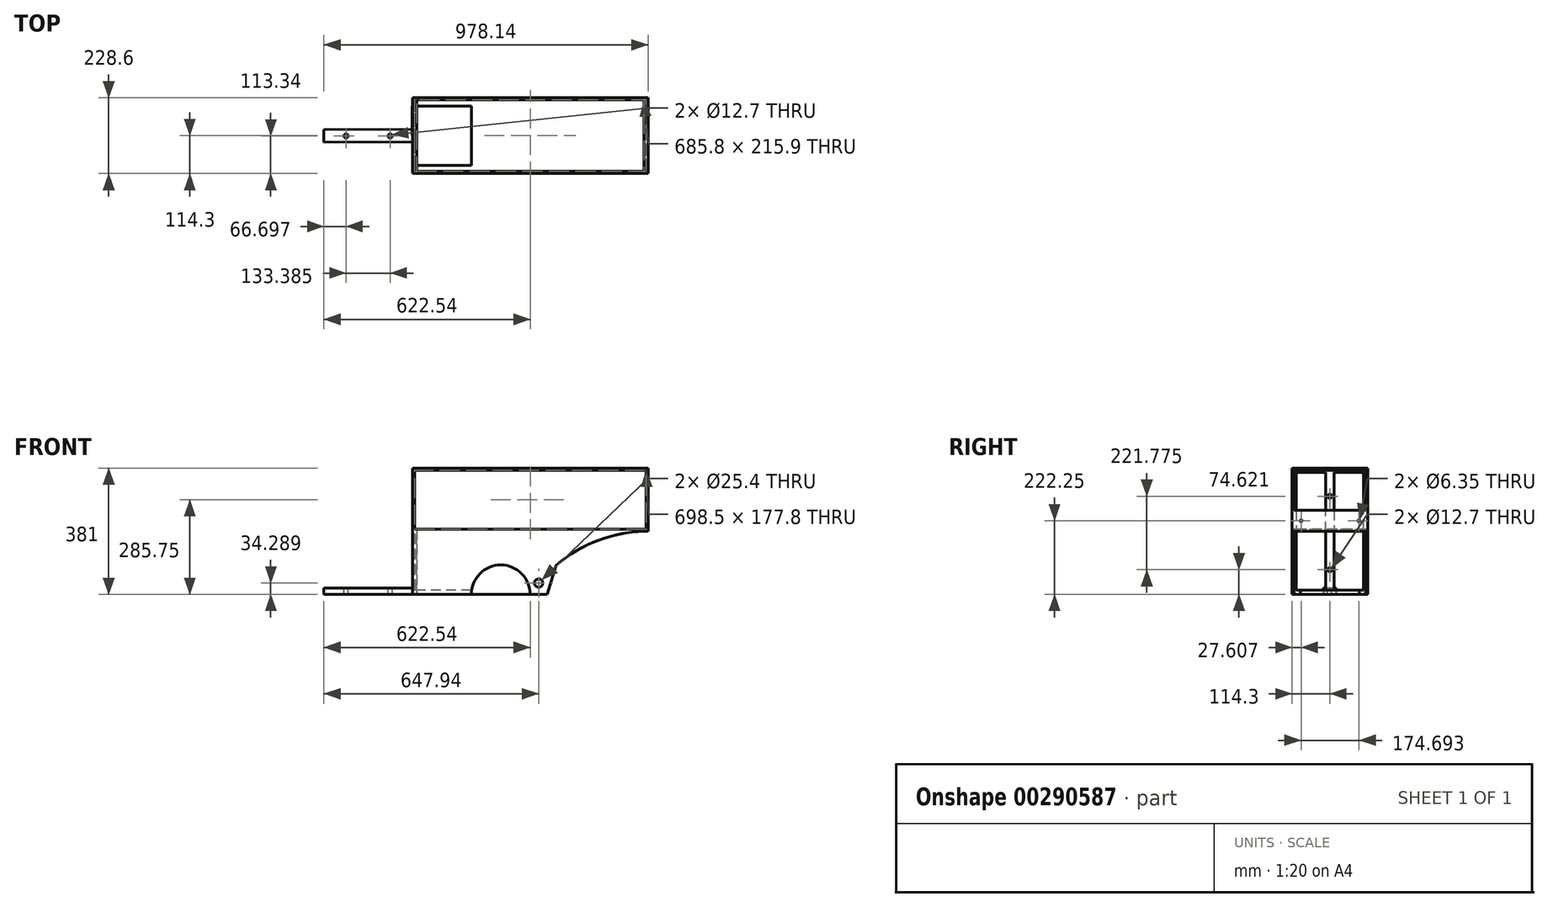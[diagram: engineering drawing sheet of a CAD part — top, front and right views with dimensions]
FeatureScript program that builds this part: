
annotation { "Feature Type Name" : "Feature", "Feature Type Description" : "" }
export const myFeature = defineFeature(function(context is Context, id is Id, definition is map)
    precondition{}
    {
        {
            var Q0;
            Q0=qCreatedBy(makeId("Top.planeOp"),FACE);
            var sketch = newSketch(context, id + "F0", { "sketchPlane" : qUnion([Q0])});
            skLineSegment(sketch, "E0.bottom", {"start": v(-355.6, 114.3) * mm, "end": v(355.6, 114.3) * mm});
            skLineSegment(sketch, "E0.top", {"start": v(-355.6, -114.3) * mm, "end": v(355.6, -114.3) * mm});
            skLineSegment(sketch, "E0.left", {"start": v(-355.6, 114.3) * mm, "end": v(-355.6, -114.3) * mm});
            skLineSegment(sketch, "E0.right", {"start": v(355.6, 114.3) * mm, "end": v(355.6, -114.3) * mm});
            skPoint(sketch, "E0.middle", {"position": v(0, 0) * mm});
            skLineSegment(sketch, "E1.bottom", {"start": v(-342.9, 107.95) * mm, "end": v(342.9, 107.95) * mm});
            skLineSegment(sketch, "E1.top", {"start": v(-342.9, -107.95) * mm, "end": v(342.9, -107.95) * mm});
            skLineSegment(sketch, "E1.left", {"start": v(-342.9, 107.95) * mm, "end": v(-342.9, -107.95) * mm});
            skLineSegment(sketch, "E1.right", {"start": v(342.9, 107.95) * mm, "end": v(342.9, -107.95) * mm});
            skSolve(sketch);
        }
        {
            var Q0;
            Q0=makeQuery(id+"F0.imprint","IMPRINT",FACE,{"disambiguationData":[TD([[makeQuery(id+"F0.imprint","IMPRINT",EDGE,{"derivedFrom":sQuery(id+"F0.wireOp",EDGE,"E0.bottom")}),-1.0]])]});
            extrude(context, id + "F1", {"entities" : qUnion([Q0]), "depth" : 381 * mm});
        }
        {
            var Q0;
            Q0=makeQuery(id+"F1.opExtrude","SWEPT_FACE",FACE,{"disambiguationData":[OSD([sQuery(id+"F0.wireOp",EDGE,"E0.top")])]});
            var sketch = newSketch(context, id + "F2", { "sketchPlane" : qUnion([Q0])});
            skLineSegment(sketch, "E2", {"start": v(-355.6, 381) * mm, "end": v(-355.6, 190.5) * mm, "construction": true});
            skLineSegment(sketch, "E3", {"start": v(-355.6, 190.5) * mm, "end": v(355.6, 190.5) * mm, "construction": true});
            skLineSegment(sketch, "E4", {"start": v(355.6, 190.5) * mm, "end": v(355.6, 381) * mm, "construction": true});
            skLineSegment(sketch, "E5", {"start": v(355.6, 381) * mm, "end": v(355.6, 0) * mm, "construction": true});
            skLineSegment(sketch, "E6", {"start": v(355.6, 0) * mm, "end": v(-355.6, 0) * mm, "construction": true});
            skLineSegment(sketch, "E7", {"start": v(-355.6, 0) * mm, "end": v(-355.6, 190.5) * mm, "construction": true});
            skLineSegment(sketch, "E8", {"start": v(-355.6, 381) * mm, "end": v(355.6, 381) * mm, "construction": true});
            skLineSegment(sketch, "E9", {"start": v(0, 190.5) * mm, "end": v(0, 381) * mm, "construction": true});
            skLineSegment(sketch, "E10", {"start": v(0, 381) * mm, "end": v(0, 0) * mm, "construction": true});
            skLineSegment(sketch, "E11", {"start": v(0, 0) * mm, "end": v(-355.6, 0) * mm, "construction": true});
            skLineSegment(sketch, "E12", {"start": v(-177.8, 0) * mm, "end": v(-177.8, 381) * mm, "construction": true});
            skLineSegment(sketch, "E13", {"start": v(-177.8, 381) * mm, "end": v(0, 381) * mm, "construction": true});
            skLineSegment(sketch, "E14", {"start": v(355.6, 381) * mm, "end": v(0, 381) * mm, "construction": true});
            skLineSegment(sketch, "E15", {"start": v(177.8, 381) * mm, "end": v(177.8, 0) * mm, "construction": true});
            skArc(sketch, "E16", {"start": v(355.6, 190.5) * mm, "mid": v(153.9, 139.87) * mm, "end": v(0, 0) * mm});
            skLineSegment(sketch, "E17.bottom", {"start": v(-349.25, 374.65) * mm, "end": v(349.25, 374.65) * mm});
            skLineSegment(sketch, "E17.top", {"start": v(-349.25, 238.03) * mm, "end": v(349.25, 238.03) * mm});
            skLineSegment(sketch, "E17.left", {"start": v(-349.25, 374.65) * mm, "end": v(-349.25, 238.03) * mm});
            skLineSegment(sketch, "E17.right", {"start": v(349.25, 374.65) * mm, "end": v(349.25, 238.03) * mm});
            skSolve(sketch);
        }
        {
            var Q0;
            Q0=makeQuery(id+"F2.imprint","IMPRINT",FACE,{"disambiguationData":[TD([[makeQuery(id+"F2.imprint","IMPRINT",EDGE,{"derivedFrom":sQuery(id+"F2.wireOp",EDGE,"E17.bottom")}),-1.0]])]});
            extrude(context, id + "F3", {"entities" : qUnion([Q0]), "operationType" : NewBodyOperationType.REMOVE, "endBound" : BoundingType.SYMMETRIC, "oppositeDirection" : true, "depth" : 381 * mm});
        }
        {
            var Q0;
            {var subQ0=sQuery(id+"F2.wireOp",EDGE,"E16");Q0=makeQuery(id+"F2.imprint","IMPRINT",FACE,{"disambiguationData":[TD([[makeQuery(id+"F2.imprint","IMPRINT",EDGE,{"derivedFrom":subQ0}),1.0]])]});}
            extrude(context, id + "F4", {"entities" : qUnion([Q0]), "operationType" : NewBodyOperationType.REMOVE, "endBound" : BoundingType.SYMMETRIC, "oppositeDirection" : true, "depth" : 508 * mm});
        }
        {
            var Q0;
            Q0=makeQuery(id+"F1.opExtrude","SWEPT_FACE",FACE,{"disambiguationData":[OSD([sQuery(id+"F0.wireOp",EDGE,"E0.left")])]});
            var sketch = newSketch(context, id + "F5", { "sketchPlane" : qUnion([Q0])});
            skLineSegment(sketch, "E18.bottom", {"start": v(-101.6, 368.3) * mm, "end": v(101.6, 368.3) * mm});
            skLineSegment(sketch, "E18.top", {"start": v(-101.6, 12.7) * mm, "end": v(101.6, 12.7) * mm});
            skLineSegment(sketch, "E18.left", {"start": v(-101.6, 368.3) * mm, "end": v(-101.6, 12.7) * mm});
            skLineSegment(sketch, "E18.right", {"start": v(101.6, 368.3) * mm, "end": v(101.6, 12.7) * mm});
            skPoint(sketch, "E18.middle", {"position": v(0, 190.5) * mm});
            skSolve(sketch);
        }
        {
            var Q0;
            Q0 = qSketchRegion(id + "F5", true);
            extrude(context, id + "F6", {"entities" : qUnion([Q0]), "operationType" : NewBodyOperationType.REMOVE, "oppositeDirection" : true, "depth" : 25.4 * mm});
        }
        {
            var Q0;
            Q0=qCreatedBy(makeId("Top.planeOp"),FACE);
            var sketch = newSketch(context, id + "F7", { "sketchPlane" : qUnion([Q0])});
            skLineSegment(sketch, "E19", {"start": v(-355.45, -89.34) * mm, "end": v(0, -89.34) * mm, "construction": true});
            skLineSegment(sketch, "E20", {"start": v(0, -89.34) * mm, "end": v(0, 88.7) * mm, "construction": true});
            skLineSegment(sketch, "E21", {"start": v(0, 88.7) * mm, "end": v(-356.09, 88.7) * mm, "construction": true});
            skLineSegment(sketch, "E22", {"start": v(-356.09, 88.7) * mm, "end": v(-355.45, -89.34) * mm, "construction": true});
            skLineSegment(sketch, "E23", {"start": v(-177.72, -89.34) * mm, "end": v(-177.72, 88.7) * mm, "construction": true});
            skLineSegment(sketch, "E24", {"start": v(-356.09, 88.7) * mm, "end": v(-177.72, 88.7) * mm});
            skLineSegment(sketch, "E25", {"start": v(-177.72, -89.34) * mm, "end": v(-355.45, -89.34) * mm});
            skLineSegment(sketch, "E26", {"start": v(-356.09, 88.7) * mm, "end": v(-355.45, -89.34) * mm});
            skLineSegment(sketch, "E27", {"start": v(-177.72, -89.34) * mm, "end": v(-177.72, 88.7) * mm});
            skLineSegment(sketch, "E28", {"start": v(0, 88.7) * mm, "end": v(0, -89.34) * mm});
            skLineSegment(sketch, "E29", {"start": v(-177.72, -89.34) * mm, "end": v(0, -89.34) * mm});
            skLineSegment(sketch, "E30", {"start": v(0, 88.7) * mm, "end": v(-177.72, 88.7) * mm});
            skSolve(sketch);
        }
        {
            var Q0;
            Q0=makeQuery(id+"F7.imprint","IMPRINT",FACE,{"disambiguationData":[TD([[makeQuery(id+"F7.imprint","IMPRINT",EDGE,{"derivedFrom":sQuery(id+"F7.wireOp",EDGE,"E24")}),-1.0]])]});
            extrude(context, id + "F8", {"entities" : qUnion([Q0]), "operationType" : NewBodyOperationType.ADD, "depth" : 12.7 * mm});
        }
        {
            var Q0;
            Q0=makeQuery(id+"F1.opExtrude","SWEPT_FACE",FACE,{"disambiguationData":[OSD([sQuery(id+"F0.wireOp",EDGE,"E0.top")])]});
            var sketch = newSketch(context, id + "F9", { "sketchPlane" : qUnion([Q0])});
            skLineSegment(sketch, "E31.bottom", {"start": v(-349.25, 238.03) * mm, "end": v(349.25, 238.03) * mm});
            skLineSegment(sketch, "E31.top", {"start": v(-349.25, 196.85) * mm, "end": v(349.25, 196.85) * mm});
            skLineSegment(sketch, "E31.left", {"start": v(-349.25, 238.03) * mm, "end": v(-349.25, 196.85) * mm});
            skLineSegment(sketch, "E31.right", {"start": v(349.25, 238.03) * mm, "end": v(349.25, 196.85) * mm});
            skSolve(sketch);
        }
        {
            var Q0;
            Q0=makeQuery(id+"F9.imprint","IMPRINT",FACE,{"disambiguationData":[TD([[makeQuery(id+"F9.imprint","IMPRINT",EDGE,{"derivedFrom":sQuery(id+"F9.wireOp",EDGE,"E31.bottom")}),1.0]])]});
            var Q1;
            Q1=makeQuery(id+"F9.imprint","IMPRINT",FACE,{"disambiguationData":[TD([[makeQuery(id+"F9.imprint","IMPRINT",EDGE,{"derivedFrom":sQuery(id+"F9.wireOp",EDGE,"E31.bottom")}),-1.0]])]});
            extrude(context, id + "F10", {"entities" : qUnion([Q0, Q1]), "operationType" : NewBodyOperationType.REMOVE, "oppositeDirection" : true, "depth" : 381 * mm});
        }
        {
            var Q0;
            Q0=makeQuery(id+"F1.opExtrude","SWEPT_FACE",FACE,{"disambiguationData":[OSD([sQuery(id+"F0.wireOp",EDGE,"E0.top")])]});
            var sketch = newSketch(context, id + "F11", { "sketchPlane" : qUnion([Q0])});
            skLineSegment(sketch, "E32", {"start": v(-177.8, 0) * mm, "end": v(0, 0) * mm, "construction": true});
            skLineSegment(sketch, "E33", {"start": v(0, 0) * mm, "end": v(-88.9, 0) * mm, "construction": true});
            skLineSegment(sketch, "E34", {"start": v(-88.9, 0) * mm, "end": v(-88.9, -79.32) * mm, "construction": true});
            skArc(sketch, "E35", {"start": v(0, 0) * mm, "mid": v(-88.9, 88.9) * mm, "end": v(-177.8, 0) * mm});
            skSolve(sketch);
        }
        {
            var Q0;
            {var subQ0=sQuery(id+"F11.wireOp",EDGE,"E35");Q0=makeQuery(id+"F11.imprint","IMPRINT",FACE,{"disambiguationData":[TD([[makeQuery(id+"F11.imprint","IMPRINT",EDGE,{"derivedFrom":subQ0}),1.0]])]});}
            extrude(context, id + "F12", {"entities" : qUnion([Q0]), "operationType" : NewBodyOperationType.REMOVE, "oppositeDirection" : true, "depth" : 25.4 * mm});
        }
        {
            var Q0;
            Q0=makeQuery(id+"F1.opExtrude","SWEPT_FACE",FACE,{"disambiguationData":[OSD([sQuery(id+"F0.wireOp",EDGE,"E0.left")])]});
            var sketch = newSketch(context, id + "F13", { "sketchPlane" : qUnion([Q0])});
            skLineSegment(sketch, "E36", {"start": v(0, 381) * mm, "end": v(0, 329.2) * mm, "construction": true});
            skLineSegment(sketch, "E37", {"start": v(-114.3, 381) * mm, "end": v(0, 381) * mm, "construction": true});
            skLineSegment(sketch, "E38", {"start": v(0, 400.9) * mm, "end": v(-114.3, 400.9) * mm, "construction": true});
            skLineSegment(sketch, "E39", {"start": v(-114.3, 400.9) * mm, "end": v(-114.3, 381) * mm, "construction": true});
            skLineSegment(sketch, "E40", {"start": v(0, 381) * mm, "end": v(0, 400.9) * mm, "construction": true});
            skLineSegment(sketch, "E41", {"start": v(114.3, 400.9) * mm, "end": v(114.3, 381) * mm, "construction": true});
            skLineSegment(sketch, "E42", {"start": v(114.3, 381) * mm, "end": v(114.3, 400.9) * mm, "construction": true});
            skLineSegment(sketch, "E43", {"start": v(0, 400.9) * mm, "end": v(114.3, 400.9) * mm, "construction": true});
            skLineSegment(sketch, "E44", {"start": v(0, 381) * mm, "end": v(114.3, 381) * mm, "construction": true});
            skLineSegment(sketch, "E45", {"start": v(-12.7, 400.9) * mm, "end": v(-12.7, 417.67) * mm, "construction": true});
            skLineSegment(sketch, "E46", {"start": v(-12.7, 417.67) * mm, "end": v(-114.3, 417.67) * mm, "construction": true});
            skLineSegment(sketch, "E47", {"start": v(-114.3, 417.67) * mm, "end": v(-114.3, 400.9) * mm, "construction": true});
            skLineSegment(sketch, "E48", {"start": v(114.3, 417.67) * mm, "end": v(114.3, 400.9) * mm, "construction": true});
            skLineSegment(sketch, "E49", {"start": v(12.7, 417.67) * mm, "end": v(12.7, 400.9) * mm, "construction": true});
            skLineSegment(sketch, "E50", {"start": v(12.7, 417.67) * mm, "end": v(114.3, 417.67) * mm, "construction": true});
            skLineSegment(sketch, "E51", {"start": v(-12.7, 400.9) * mm, "end": v(-12.7, 193.03) * mm, "construction": true});
            skLineSegment(sketch, "E52", {"start": v(-12.7, 193.03) * mm, "end": v(12.7, 193.03) * mm, "construction": true});
            skLineSegment(sketch, "E53", {"start": v(12.7, 193.03) * mm, "end": v(12.7, 400.9) * mm, "construction": true});
            skLineSegment(sketch, "E54", {"start": v(-12.7, 381) * mm, "end": v(-12.7, 0) * mm});
            skLineSegment(sketch, "E55", {"start": v(-12.7, 0) * mm, "end": v(12.7, 0) * mm});
            skLineSegment(sketch, "E56", {"start": v(12.7, 0) * mm, "end": v(12.7, 381) * mm});
            skLineSegment(sketch, "E57", {"start": v(-12.7, 381) * mm, "end": v(12.7, 381) * mm});
            skSolve(sketch);
        }
        {
            var Q0;
            {var subQ0=sQuery(id+"F13.wireOp",EDGE,"E55");Q0=makeQuery(id+"F13.imprint","IMPRINT",FACE,{"disambiguationData":[TD([[makeQuery(id+"F13.imprint","IMPRINT",EDGE,{"derivedFrom":subQ0}),1.0]])]});}
            extrude(context, id + "F14", {"entities" : qUnion([Q0]), "operationType" : NewBodyOperationType.ADD, "oppositeDirection" : true, "depth" : 6.35 * mm});
        }
        {
            var Q0;
            Q0=makeQuery(id+"F1.opExtrude","SWEPT_FACE",FACE,{"disambiguationData":[OSD([sQuery(id+"F0.wireOp",EDGE,"E0.right")])]});
            var sketch = newSketch(context, id + "F15", { "sketchPlane" : qUnion([Q0])});
            skLineSegment(sketch, "E58.bottom", {"start": v(-107.95, 374.65) * mm, "end": v(107.95, 374.65) * mm});
            skLineSegment(sketch, "E58.top", {"start": v(-107.95, 254) * mm, "end": v(107.95, 254) * mm});
            skLineSegment(sketch, "E58.left", {"start": v(-107.95, 374.65) * mm, "end": v(-107.95, 254) * mm});
            skLineSegment(sketch, "E58.right", {"start": v(107.95, 374.65) * mm, "end": v(107.95, 254) * mm});
            skSolve(sketch);
        }
        {
            var Q0;
            Q0=makeQuery(id+"F15.imprint","IMPRINT",FACE,{"disambiguationData":[TD([[makeQuery(id+"F15.imprint","IMPRINT",EDGE,{"derivedFrom":sQuery(id+"F15.wireOp",EDGE,"E58.bottom")}),-1.0]])]});
            extrude(context, id + "F16", {"entities" : qUnion([Q0]), "operationType" : NewBodyOperationType.REMOVE, "oppositeDirection" : true, "depth" : 25.4 * mm});
        }
        {
            var Q0;
            Q0=makeQuery(id+"F1.opExtrude","SWEPT_FACE",FACE,{"disambiguationData":[OSD([sQuery(id+"F0.wireOp",EDGE,"E0.right")])]});
            var sketch = newSketch(context, id + "F17", { "sketchPlane" : qUnion([Q0])});
            skLineSegment(sketch, "E59", {"start": v(-107.95, 254) * mm, "end": v(-107.95, 190.5) * mm, "construction": true});
            skLineSegment(sketch, "E60", {"start": v(-107.95, 190.5) * mm, "end": v(107.95, 190.5) * mm, "construction": true});
            skLineSegment(sketch, "E61", {"start": v(107.95, 190.5) * mm, "end": v(107.95, 254) * mm, "construction": true});
            skLineSegment(sketch, "E62", {"start": v(107.95, 254) * mm, "end": v(-107.95, 254) * mm, "construction": true});
            skLineSegment(sketch, "E63", {"start": v(-107.95, 222.25) * mm, "end": v(107.95, 222.25) * mm, "construction": true});
            skLineSegment(sketch, "E64", {"start": v(107.95, 222.25) * mm, "end": v(-101.6, 222.25) * mm, "construction": true});
            skLineSegment(sketch, "E65", {"start": v(-101.6, 222.25) * mm, "end": v(-101.6, 239.75) * mm, "construction": true});
            skLineSegment(sketch, "E66", {"start": v(-101.6, 239.75) * mm, "end": v(101.6, 239.75) * mm, "construction": true});
            skLineSegment(sketch, "E67", {"start": v(101.6, 239.75) * mm, "end": v(101.6, 222.25) * mm, "construction": true});
            skPoint(sketch, "E68", {"position": v(-101.6, 222.25) * mm});
            skPoint(sketch, "E69", {"position": v(101.6, 222.25) * mm});
            skPoint(sketch, "E70", {"position": v(-86.7, 222.25) * mm});
            skPoint(sketch, "E71", {"position": v(88, 222.25) * mm});
            skSolve(sketch);
        }
        {
            var Q0;
            Q0=sQuery(id+"F17.wireOp",VERTEX,"E70");
            var Q1;
            Q1=sQuery(id+"F17.wireOp",VERTEX,"E71");
            var Q2;
            Q2=makeQuery(id+"F1.opExtrude","SWEPT_BODY",BODY,{"disambiguationData":[OSD([sQuery(id+"F0.wireOp",EDGE,"E0.bottom"),sQuery(id+"F0.wireOp",EDGE,"E0.top"),sQuery(id+"F0.wireOp",EDGE,"E0.left"),sQuery(id+"F0.wireOp",EDGE,"E0.right"),sQuery(id+"F0.wireOp",EDGE,"E1.bottom"),sQuery(id+"F0.wireOp",EDGE,"E1.top"),sQuery(id+"F0.wireOp",EDGE,"E1.left"),sQuery(id+"F0.wireOp",EDGE,"E1.right")])]});
            hole(context, id + "F18", {"style" : HoleStyle.SIMPLE, "endStyle" : HoleEndStyle.THROUGH, "holeDiameter" : 6.35 * mm, "tappedDepth" : 12.7 * mm, "tapClearance" : 3, "locations" : qUnion([Q0, Q1]), "scope" : qUnion([Q2])});
        }
        {
            var Q0;
            Q0=makeQuery(id+"F14.boolean.opBoolean","MERGE",FACE,{"derivedFrom":[makeQuery(id+"F1.opExtrude","SWEPT_FACE",FACE,{"disambiguationData":[OSD([sQuery(id+"F0.wireOp",EDGE,"E0.left")])]}),makeQuery(id+"F14.opExtrude","CAP_FACE",FACE,{"disambiguationData":[OSD([sQuery(id+"F5.wireOp",EDGE,"E18.bottom"),sQuery(id+"F13.wireOp",EDGE,"E54"),sQuery(id+"F13.wireOp",EDGE,"E55"),sQuery(id+"F13.wireOp",EDGE,"E56")])],"isStart":true})]});
            var sketch = newSketch(context, id + "F19", { "sketchPlane" : qUnion([Q0])});
            skPoint(sketch, "E72", {"position": v(0, 296.4) * mm});
            skPoint(sketch, "E73", {"position": v(0, 74.62) * mm});
            skSolve(sketch);
        }
        {
            var Q0;
            Q0=sQuery(id+"F19.wireOp",VERTEX,"E72");
            var Q1;
            Q1=sQuery(id+"F19.wireOp",VERTEX,"E73");
            var Q2;
            Q2=makeQuery(id+"F1.opExtrude","SWEPT_BODY",BODY,{"disambiguationData":[OSD([sQuery(id+"F0.wireOp",EDGE,"E0.bottom"),sQuery(id+"F0.wireOp",EDGE,"E0.top"),sQuery(id+"F0.wireOp",EDGE,"E0.left"),sQuery(id+"F0.wireOp",EDGE,"E0.right"),sQuery(id+"F0.wireOp",EDGE,"E1.bottom"),sQuery(id+"F0.wireOp",EDGE,"E1.top"),sQuery(id+"F0.wireOp",EDGE,"E1.left"),sQuery(id+"F0.wireOp",EDGE,"E1.right")])]});
            hole(context, id + "F20", {"style" : HoleStyle.SIMPLE, "endStyle" : HoleEndStyle.THROUGH, "holeDiameter" : 12.7 * mm, "tappedDepth" : 12.7 * mm, "tapClearance" : 3, "locations" : qUnion([Q0, Q1]), "scope" : qUnion([Q2])});
        }
        {
            var Q0;
            Q0=makeQuery(id+"F1.opExtrude","SWEPT_FACE",FACE,{"disambiguationData":[OSD([sQuery(id+"F0.wireOp",EDGE,"E0.top")])]});
            var sketch = newSketch(context, id + "F21", { "sketchPlane" : qUnion([Q0])});
            skLineSegment(sketch, "E74", {"start": v(0, 0) * mm, "end": v(50.8, 0) * mm, "construction": true});
            skLineSegment(sketch, "E75", {"start": v(50.8, 0) * mm, "end": v(77.96, 87.96) * mm, "construction": true});
            skLineSegment(sketch, "E76", {"start": v(25.4, 0) * mm, "end": v(25.4, 34.32) * mm, "construction": true});
            skLineSegment(sketch, "E77", {"start": v(0, 0) * mm, "end": v(50.8, 0) * mm});
            skLineSegment(sketch, "E78", {"start": v(77.96, 87.96) * mm, "end": v(50.8, 0) * mm});
            skPoint(sketch, "E79", {"position": v(25.4, 34.32) * mm});
            skSolve(sketch);
        }
        {
            var Q0;
            {var subQ0=sQuery(id+"F21.wireOp",EDGE,"E77");Q0=makeQuery(id+"F21.imprint","IMPRINT",FACE,{"disambiguationData":[TD([[makeQuery(id+"F21.imprint","IMPRINT",EDGE,{"derivedFrom":subQ0}),1.0]])]});}
            extrude(context, id + "F22", {"entities" : qUnion([Q0]), "operationType" : NewBodyOperationType.ADD, "oppositeDirection" : true, "depth" : 6.35 * mm});
        }
        {
            var Q0;
            Q0=makeQuery(id+"F1.opExtrude","SWEPT_FACE",FACE,{"disambiguationData":[OSD([sQuery(id+"F0.wireOp",EDGE,"E0.bottom")])]});
            var sketch = newSketch(context, id + "F23", { "sketchPlane" : qUnion([Q0])});
            skLineSegment(sketch, "E80", {"start": v(-77.65, 87.7) * mm, "end": v(-50.6, 0) * mm});
            skLineSegment(sketch, "E81", {"start": v(-50.6, 0) * mm, "end": v(0, 0) * mm});
            skPoint(sketch, "E82", {"position": v(-25.29, 34.18) * mm});
            skSolve(sketch);
        }
        {
            var Q0;
            {var subQ0=sQuery(id+"F23.wireOp",EDGE,"E80");Q0=makeQuery(id+"F23.imprint","IMPRINT",FACE,{"disambiguationData":[TD([[makeQuery(id+"F23.imprint","IMPRINT",EDGE,{"derivedFrom":subQ0}),1.0]])]});}
            extrude(context, id + "F24", {"entities" : qUnion([Q0]), "operationType" : NewBodyOperationType.ADD, "oppositeDirection" : true, "depth" : 6.35 * mm});
        }
        {
            var Q0;
            {var subQ0=sQuery(id+"F0.wireOp",EDGE,"E0.bottom");Q0=makeQuery(id+"F24.boolean.opBoolean","MERGE",FACE,{"derivedFrom":[makeQuery(id+"F1.opExtrude","SWEPT_FACE",FACE,{"disambiguationData":[OSD([subQ0])]}),makeQuery(id+"F24.opExtrude","CAP_FACE",FACE,{"disambiguationData":[OSD([subQ0,sQuery(id+"F2.wireOp",EDGE,"E16"),sQuery(id+"F23.wireOp",EDGE,"E80"),sQuery(id+"F23.wireOp",EDGE,"E81")])],"isStart":true})]});}
            var sketch = newSketch(context, id + "F25", { "sketchPlane" : qUnion([Q0])});
            skPoint(sketch, "E83", {"position": v(-25.4, 34.29) * mm});
            skSolve(sketch);
        }
        {
            var Q0;
            Q0=sQuery(id+"F25.wireOp",VERTEX,"E83");
            var Q1;
            Q1=makeQuery(id+"F1.opExtrude","SWEPT_BODY",BODY,{"disambiguationData":[OSD([sQuery(id+"F0.wireOp",EDGE,"E0.bottom"),sQuery(id+"F0.wireOp",EDGE,"E0.top"),sQuery(id+"F0.wireOp",EDGE,"E0.left"),sQuery(id+"F0.wireOp",EDGE,"E0.right"),sQuery(id+"F0.wireOp",EDGE,"E1.bottom"),sQuery(id+"F0.wireOp",EDGE,"E1.top"),sQuery(id+"F0.wireOp",EDGE,"E1.left"),sQuery(id+"F0.wireOp",EDGE,"E1.right")])]});
            hole(context, id + "F26", {"style" : HoleStyle.SIMPLE, "endStyle" : HoleEndStyle.THROUGH, "holeDiameter" : 25.4 * mm, "tappedDepth" : 12.7 * mm, "tapClearance" : 3, "locations" : qUnion([Q0]), "scope" : qUnion([Q1])});
        }
        {
            var Q0;
            Q0=makeQuery(id+"F24.boolean.opBoolean","MERGE",FACE,{"derivedFrom":[makeQuery(id+"F8.boolean.opBoolean","MERGE",FACE,{"derivedFrom":[makeQuery(id+"F1.opExtrude","CAP_FACE",FACE,{"disambiguationData":[OSD([sQuery(id+"F0.wireOp",EDGE,"E0.bottom"),sQuery(id+"F0.wireOp",EDGE,"E0.top"),sQuery(id+"F0.wireOp",EDGE,"E0.left"),sQuery(id+"F0.wireOp",EDGE,"E0.right"),sQuery(id+"F0.wireOp",EDGE,"E1.bottom"),sQuery(id+"F0.wireOp",EDGE,"E1.top"),sQuery(id+"F0.wireOp",EDGE,"E1.left"),sQuery(id+"F0.wireOp",EDGE,"E1.right")])],"isStart":true}),makeQuery(id+"F8.opExtrude","CAP_FACE",FACE,{"disambiguationData":[OSD([sQuery(id+"F7.wireOp",EDGE,"E24"),sQuery(id+"F7.wireOp",EDGE,"E25"),sQuery(id+"F7.wireOp",EDGE,"E26"),sQuery(id+"F7.wireOp",EDGE,"E27")])],"isStart":true})]}),makeQuery(id+"F24.opExtrude","SWEPT_FACE",FACE,{"disambiguationData":[OSD([sQuery(id+"F23.wireOp",EDGE,"E81")])]})]});
            var sketch = newSketch(context, id + "F27", { "sketchPlane" : qUnion([Q0])});
            skLineSegment(sketch, "E84", {"start": v(-355.84, -19.05) * mm, "end": v(-622.54, -18.1) * mm, "construction": true});
            skLineSegment(sketch, "E85", {"start": v(-355.77, 0) * mm, "end": v(-355.7, 19.05) * mm, "construction": true});
            skLineSegment(sketch, "E86", {"start": v(-355.7, 19.05) * mm, "end": v(-416.14, 19.27) * mm, "construction": true});
            skLineSegment(sketch, "E87", {"start": v(-355.7, 19.05) * mm, "end": v(-622.54, 20) * mm, "construction": true});
            skLineSegment(sketch, "E88", {"start": v(-622.54, 20) * mm, "end": v(-622.54, -18.1) * mm, "construction": true});
            skLineSegment(sketch, "E89", {"start": v(-355.7, 19.05) * mm, "end": v(-622.54, 20) * mm});
            skLineSegment(sketch, "E90", {"start": v(-622.54, -18.1) * mm, "end": v(-355.84, -19.05) * mm});
            skLineSegment(sketch, "E91", {"start": v(-622.54, 20) * mm, "end": v(-622.54, -18.1) * mm});
            skLineSegment(sketch, "E92", {"start": v(-355.84, -19.05) * mm, "end": v(-355.7, 19.05) * mm});
            skSolve(sketch);
        }
        {
            var Q0;
            Q0=makeQuery(id+"F27.imprint","IMPRINT",FACE,{"disambiguationData":[TD([[makeQuery(id+"F27.imprint","IMPRINT",EDGE,{"derivedFrom":sQuery(id+"F27.wireOp",EDGE,"E89")}),1.0]])]});
            extrude(context, id + "F28", {"entities" : qUnion([Q0]), "operationType" : NewBodyOperationType.ADD, "oppositeDirection" : true, "depth" : 19.05 * mm});
        }
        {
            var Q0;
            Q0=makeQuery(id+"F28.opExtrude","CAP_FACE",FACE,{"disambiguationData":[OSD([sQuery(id+"F27.wireOp",EDGE,"E89"),sQuery(id+"F27.wireOp",EDGE,"E90"),sQuery(id+"F27.wireOp",EDGE,"E91"),sQuery(id+"F27.wireOp",EDGE,"E92")])],"isStart":false});
            var sketch = newSketch(context, id + "F29", { "sketchPlane" : qUnion([Q0])});
            skLineSegment(sketch, "E93", {"start": v(-622.54, -0.96) * mm, "end": v(-355.77, -0.96) * mm, "construction": true});
            skLineSegment(sketch, "E94", {"start": v(-355.77, -0.96) * mm, "end": v(-489.15, -0.96) * mm, "construction": true});
            skLineSegment(sketch, "E95", {"start": v(-489.15, -0.96) * mm, "end": v(-489.15, 18.1) * mm, "construction": true});
            skLineSegment(sketch, "E96", {"start": v(-489.15, 18.1) * mm, "end": v(-489.15, -20) * mm, "construction": true});
            skLineSegment(sketch, "E97", {"start": v(-489.15, -0.96) * mm, "end": v(-622.54, -0.96) * mm, "construction": true});
            skLineSegment(sketch, "E98", {"start": v(-555.84, -0.96) * mm, "end": v(-555.84, 18.33) * mm, "construction": true});
            skLineSegment(sketch, "E99", {"start": v(-555.84, 18.33) * mm, "end": v(-555.84, -19.77) * mm, "construction": true});
            skLineSegment(sketch, "E100", {"start": v(-555.84, -19.77) * mm, "end": v(-422.46, -19.77) * mm, "construction": true});
            skPoint(sketch, "E100.endSnap0", {"position": v(-422.46, -0.96) * mm});
            skLineSegment(sketch, "E101", {"start": v(-422.46, -19.77) * mm, "end": v(-422.46, -0.96) * mm, "construction": true});
            skLineSegment(sketch, "E102", {"start": v(-422.46, 18.81) * mm, "end": v(-422.46, -0.96) * mm, "construction": true});
            skPoint(sketch, "E103", {"position": v(-555.84, -0.96) * mm});
            skSolve(sketch);
        }
        {
            var Q0;
            Q0=sQuery(id+"F29.wireOp",VERTEX,"E103");
            var Q1;
            Q1=sQuery(id+"F29.wireOp",VERTEX,"E100.endSnap0");
            var Q2;
            Q2=makeQuery(id+"F1.opExtrude","SWEPT_BODY",BODY,{"disambiguationData":[OSD([sQuery(id+"F0.wireOp",EDGE,"E0.bottom"),sQuery(id+"F0.wireOp",EDGE,"E0.top"),sQuery(id+"F0.wireOp",EDGE,"E0.left"),sQuery(id+"F0.wireOp",EDGE,"E0.right"),sQuery(id+"F0.wireOp",EDGE,"E1.bottom"),sQuery(id+"F0.wireOp",EDGE,"E1.top"),sQuery(id+"F0.wireOp",EDGE,"E1.left"),sQuery(id+"F0.wireOp",EDGE,"E1.right")])]});
            hole(context, id + "F30", {"style" : HoleStyle.SIMPLE, "endStyle" : HoleEndStyle.THROUGH, "holeDiameter" : 12.7 * mm, "tappedDepth" : 12.7 * mm, "tapClearance" : 3, "locations" : qUnion([Q0, Q1]), "scope" : qUnion([Q2])});
        }
    });
